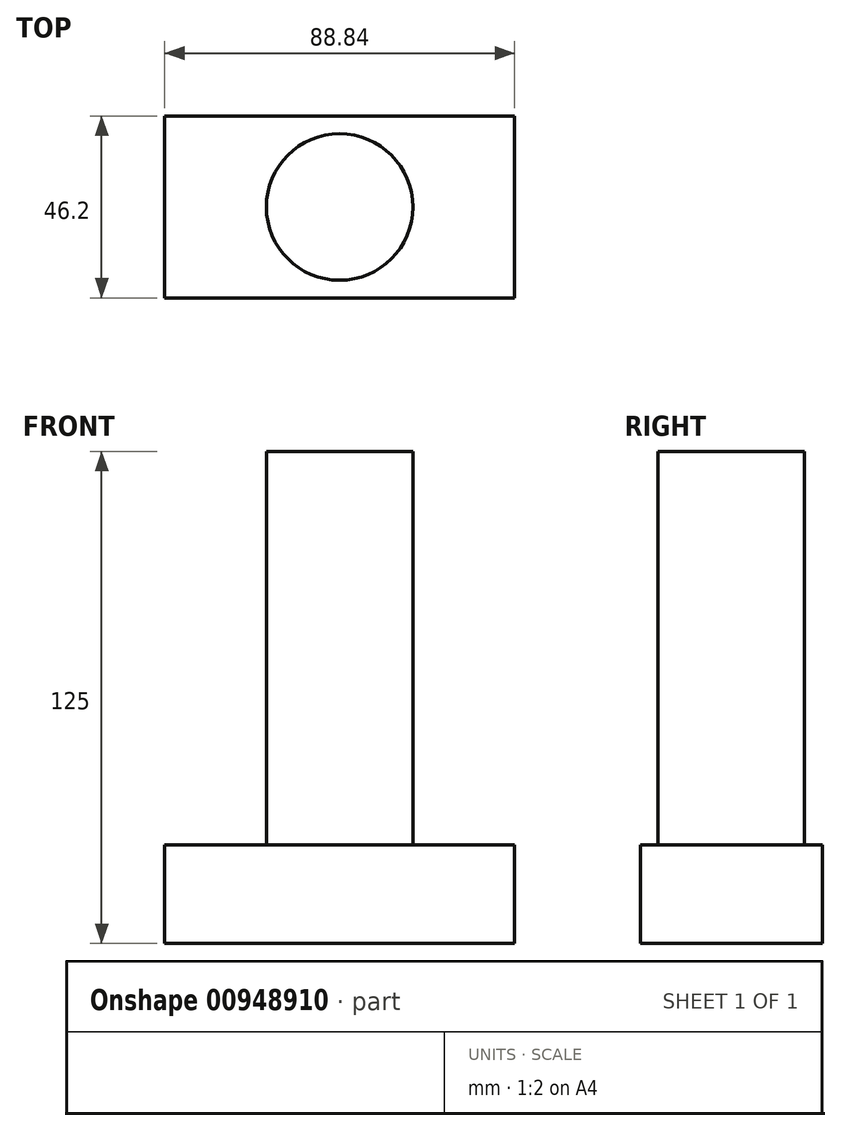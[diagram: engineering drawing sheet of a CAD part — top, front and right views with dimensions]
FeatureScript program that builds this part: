
annotation { "Feature Type Name" : "Feature", "Feature Type Description" : "" }
export const myFeature = defineFeature(function(context is Context, id is Id, definition is map)
    precondition{}
    {
        {
            var Q0;
            Q0=qCreatedBy(makeId("Top.planeOp"),FACE);
            var sketch = newSketch(context, id + "F0", { "sketchPlane" : qUnion([Q0])});
            skLineSegment(sketch, "E0.bottom", {"start": v(44.42, 23.1) * mm, "end": v(-44.42, 23.1) * mm});
            skLineSegment(sketch, "E0.top", {"start": v(44.42, -23.1) * mm, "end": v(-44.42, -23.1) * mm});
            skLineSegment(sketch, "E0.left", {"start": v(44.42, 23.1) * mm, "end": v(44.42, -23.1) * mm});
            skLineSegment(sketch, "E0.right", {"start": v(-44.42, 23.1) * mm, "end": v(-44.42, -23.1) * mm});
            skPoint(sketch, "E0.middle", {"position": v(0, 0) * mm});
            skSolve(sketch);
        }
        {
            var Q0;
            Q0=qCreatedBy(makeId("Top.planeOp"),FACE);
            var sketch = newSketch(context, id + "F1", { "sketchPlane" : qUnion([Q0])});
            skSolve(sketch);
        }
        {
            var Q0;
            Q0 = qSketchRegion(id + "F1", true);
            var Q1;
            Q1=makeQuery(id+"F0.imprint","IMPRINT",FACE,{"disambiguationData":[TD([[makeQuery(id+"F0.imprint","IMPRINT",EDGE,{"derivedFrom":sQuery(id+"F0.wireOp",EDGE,"E0.bottom")}),1.0]])]});
            extrude(context, id + "F2", {"entities" : qUnion([Q0, Q1]), "depth" : 25 * mm, "offsetDistance" : 25 * mm});
        }
        {
            var Q0;
            Q0=makeQuery(id+"F2.opExtrude","CAP_FACE",FACE,{"disambiguationData":[OSD([sQuery(id+"F0.wireOp",EDGE,"E0.bottom"),sQuery(id+"F0.wireOp",EDGE,"E0.top"),sQuery(id+"F0.wireOp",EDGE,"E0.left"),sQuery(id+"F0.wireOp",EDGE,"E0.right")])],"isStart":false});
            var sketch = newSketch(context, id + "F3", { "sketchPlane" : qUnion([Q0])});
            skCircle(sketch, "E1", {"center": v(0, 0) * mm, "radius": 18.6 * mm});
            skSolve(sketch);
        }
        {
            var Q0;
            Q0=makeQuery(id+"F3.imprint","IMPRINT",FACE,{"disambiguationData":[TD([[makeQuery(id+"F3.imprint","IMPRINT",EDGE,{"derivedFrom":sQuery(id+"F3.wireOp",EDGE,"E1")}),1.0]])]});
            extrude(context, id + "F4", {"entities" : qUnion([Q0]), "operationType" : NewBodyOperationType.ADD, "depth" : 100 * mm, "offsetDistance" : 25 * mm});
        }
    });
